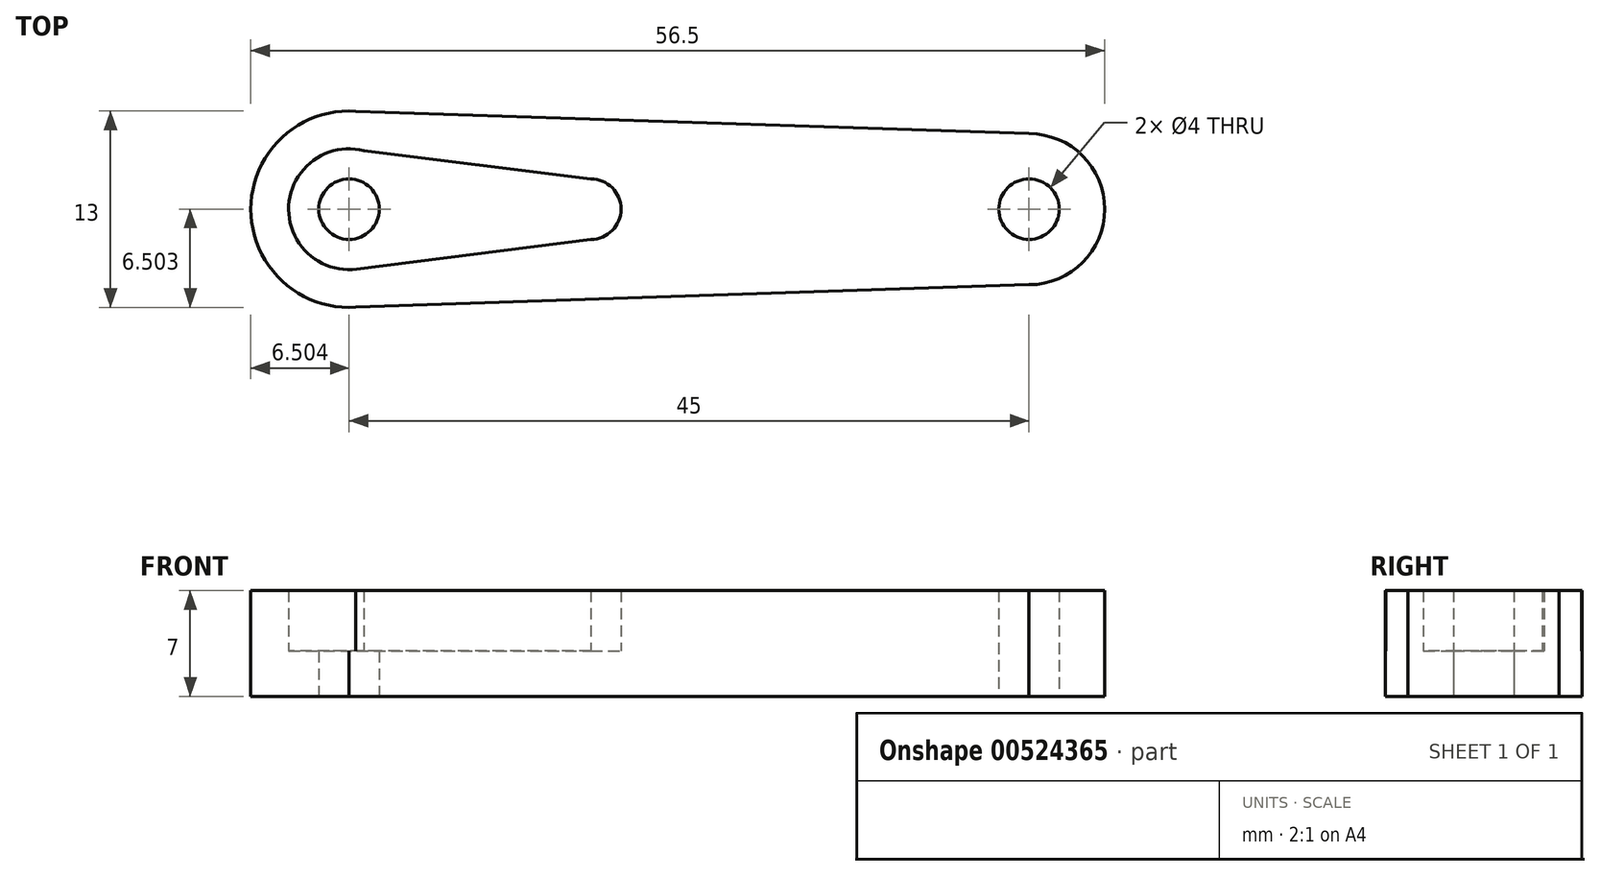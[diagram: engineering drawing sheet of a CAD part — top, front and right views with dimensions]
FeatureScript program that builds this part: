
annotation { "Feature Type Name" : "Feature", "Feature Type Description" : "" }
export const myFeature = defineFeature(function(context is Context, id is Id, definition is map)
    precondition{}
    {
        {
            var Q0;
            Q0=qCreatedBy(makeId("Top.planeOp"),FACE);
            var sketch = newSketch(context, id + "F0", { "sketchPlane" : qUnion([Q0])});
            skArc(sketch, "E0", {"start": v(10.95, 0.03) * mm, "mid": v(15.95, 5.03) * mm, "end": v(10.95, 10.03) * mm});
            skArc(sketch, "E1", {"start": v(-33.61, 11.52) * mm, "mid": v(-40.55, 5.03) * mm, "end": v(-33.61, -1.45) * mm});
            skLineSegment(sketch, "E2", {"start": v(-34.05, -1.47) * mm, "end": v(10.95, 0.03) * mm});
            skLineSegment(sketch, "E3", {"start": v(-34.05, 11.53) * mm, "end": v(10.95, 10.03) * mm});
            skCircle(sketch, "E4", {"center": v(-34.05, 5.03) * mm, "radius": 2 * mm});
            skCircle(sketch, "E5", {"center": v(10.95, 5.03) * mm, "radius": 2 * mm});
            skArc(sketch, "E6", {"start": v(-33.06, 8.9) * mm, "mid": v(-38.04, 5.28) * mm, "end": v(-33.54, 1.06) * mm});
            skArc(sketch, "E7", {"start": v(-18.05, 3.03) * mm, "mid": v(-16.05, 5.03) * mm, "end": v(-18.05, 7.03) * mm});
            skLineSegment(sketch, "E8", {"start": v(-18.05, 3.03) * mm, "end": v(-33.54, 1.06) * mm});
            skLineSegment(sketch, "E9", {"start": v(-33.06, 8.9) * mm, "end": v(-18.05, 7.03) * mm});
            skLineSegment(sketch, "E10.trimOffspring", {"start": v(10.95, 0.03) * mm, "end": v(10.95, -0.96) * mm});
            skSolve(sketch);
        }
        {
            var Q0;
            Q0=makeQuery(id+"F0.imprint","IMPRINT",FACE,{"disambiguationData":[TD([[makeQuery(id+"F0.imprint","IMPRINT",EDGE,{"derivedFrom":sQuery(id+"F0.wireOp",EDGE,"E4")}),-1.0]])]});
            var Q1;
            {var subQ1=sQuery(id+"F0.wireOp",EDGE,"E0");Q1=makeQuery(id+"F0.imprint","IMPRINT",FACE,{"disambiguationData":[TD([[makeQuery(id+"F0.imprint","IMPRINT",EDGE,{"derivedFrom":subQ1}),1.0]])]});}
            extrude(context, id + "F1", {"entities" : qUnion([Q0, Q1]), "depth" : 3 * mm, "offsetDistance" : 25 * mm});
        }
        {
            var Q0;
            Q0 = qSketchRegion(id + "F0", true);
            extrude(context, id + "F2", {"entities" : qUnion([Q0]), "operationType" : NewBodyOperationType.ADD, "depth" : 7 * mm, "offsetDistance" : 25 * mm});
        }
    });
